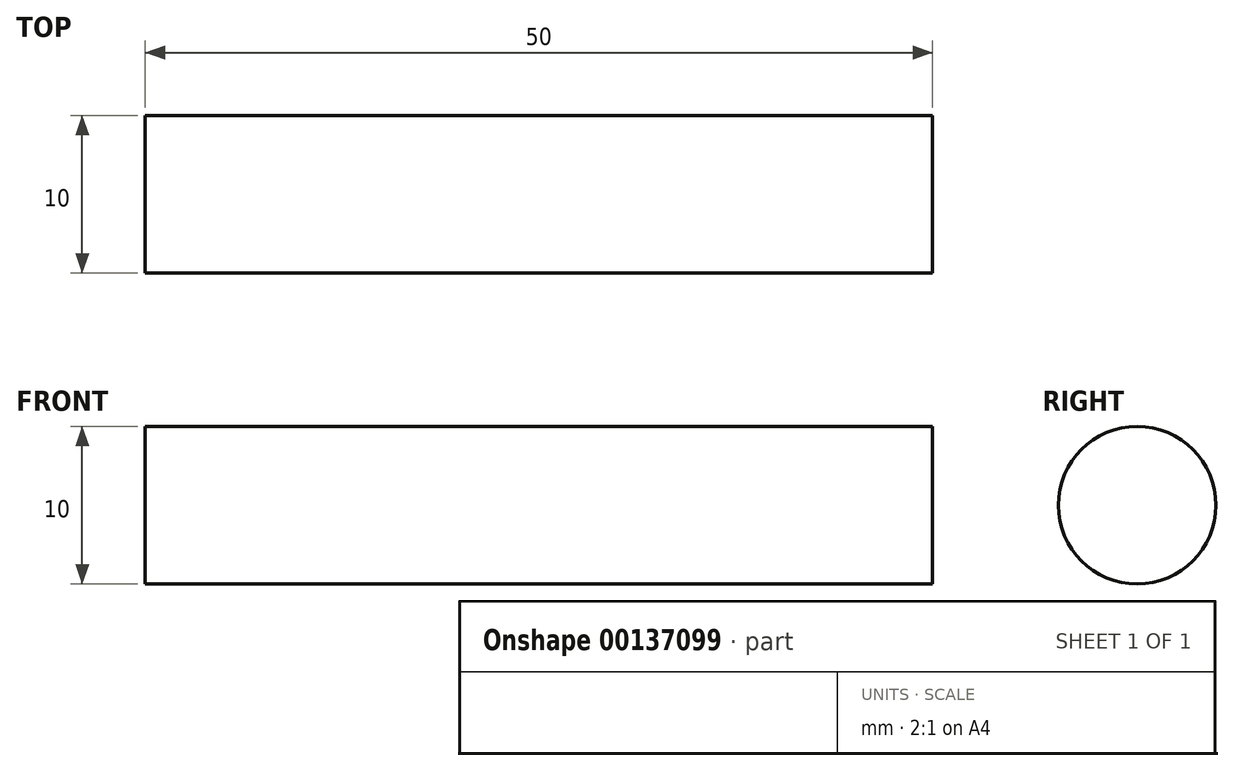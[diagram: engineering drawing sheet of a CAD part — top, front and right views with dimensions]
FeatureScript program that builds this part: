
annotation { "Feature Type Name" : "Feature", "Feature Type Description" : "" }
export const myFeature = defineFeature(function(context is Context, id is Id, definition is map)
    precondition{}
    {
        {
            var Q0;
            Q0=qCreatedBy(makeId("Right.planeOp"),FACE);
            var sketch = newSketch(context, id + "F0", { "sketchPlane" : qUnion([Q0])});
            skCircle(sketch, "E0", {"center": v(0, 0) * mm, "radius": 5 * mm});
            skSolve(sketch);
        }
        {
            var Q0;
            Q0=makeQuery(id+"F0.imprint","IMPRINT",FACE,{"disambiguationData":[TD([[makeQuery(id+"F0.imprint","IMPRINT",EDGE,{"derivedFrom":sQuery(id+"F0.wireOp",EDGE,"E0")}),1.0]])]});
            extrude(context, id + "F1", {"entities" : qUnion([Q0]), "endBound" : BoundingType.SYMMETRIC, "depth" : 50 * mm});
        }
    });
